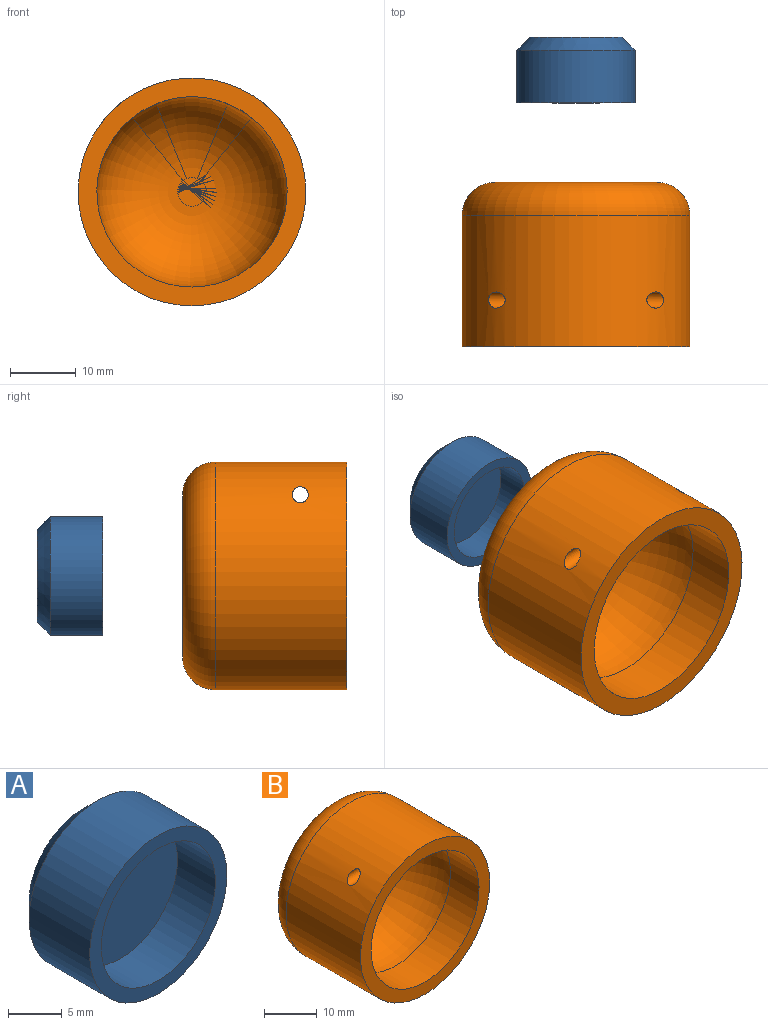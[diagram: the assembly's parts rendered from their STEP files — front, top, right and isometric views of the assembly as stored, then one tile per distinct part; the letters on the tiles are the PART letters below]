
ASSEMBLY  parts=2 mates=1
PART A: 6 faces, bbox 18.1x10x18.1 mm
  f0: cylinder r=7.54mm len=15.08mm, axis (0,1,0), area 236.9mm2, adj f2,f4
  f1: cylinder r=9.05mm len=18.1mm, axis (0,1,0), area 455mm2, adj f2,f5
  f2: plane 18.1x18.1mm, normal (0,-1,0), area 78.8mm2, adj f0,f1
  f3: plane 14.1x14.1mm, normal (0,1,0), area 156.2mm2, adj f5
  f4: plane 15.08x15.08mm, normal (0,-1,0), area 178.6mm2, adj f0
  f5: cone r=9.05mm half-angle=45deg, axis (0,-1,0), area 143.1mm2, adj f1,f3
PART B: 12 faces, bbox 37.5x25x37.5 mm
  f0: cylinder r=17.34mm len=34.69mm, axis (0,1,0), area 2165.7mm2, adj f1,f5,f6,f7
  f1: plane 34.69x34.69mm, normal (0,-1,0), area 285.3mm2, adj f0,f3
  f2: plane 24.69x24.69mm, normal (0,1,0), area 478.6mm2, adj f7
  f3: cylinder r=14.49mm len=28.98mm, axis (0,-1,0), area 684.8mm2, adj f1,f5,f6,f9,f10
  f4: plane 4.36x4.36mm, normal (0,-1,0), area 14.9mm2, adj f8,f9,f10,f11
  f5: cylinder r=1.23mm len=8.26mm, axis (1,0,0), area 37.1mm2, adj f0,f3,f8
  f6: cylinder r=1.23mm len=8.26mm, axis (1,0,0), area 37.1mm2, adj f0,f3,f11
  f7: torus R=12.34mm, axis (0,-1,0), area 766.2mm2, adj f0,f2
  f8: bspline ~12.45x11.97mm, area 54.5mm2, adj f4,f5,f9,f10
  f9: torus R=2.18mm, axis (0,-1,0), area 149.8mm2, adj f3,f4,f8,f11
  f10: torus R=2.18mm, axis (0,-1,0), area 954.6mm2, adj f3,f4,f8,f11
  f11: bspline ~12.43x11.92mm, area 58.3mm2, adj f4,f6,f9,f10
PLACE A t=(27.3,-19.82,-3.36)mm
PLACE B rot(axis=(0,-1,0),0deg) t=(-13.52,-41.93,-15.62)mm
MATE slider A.f0 <-> B.f0  axis (0,-1,0) through (-39.6,-29.82,23.25)mm
